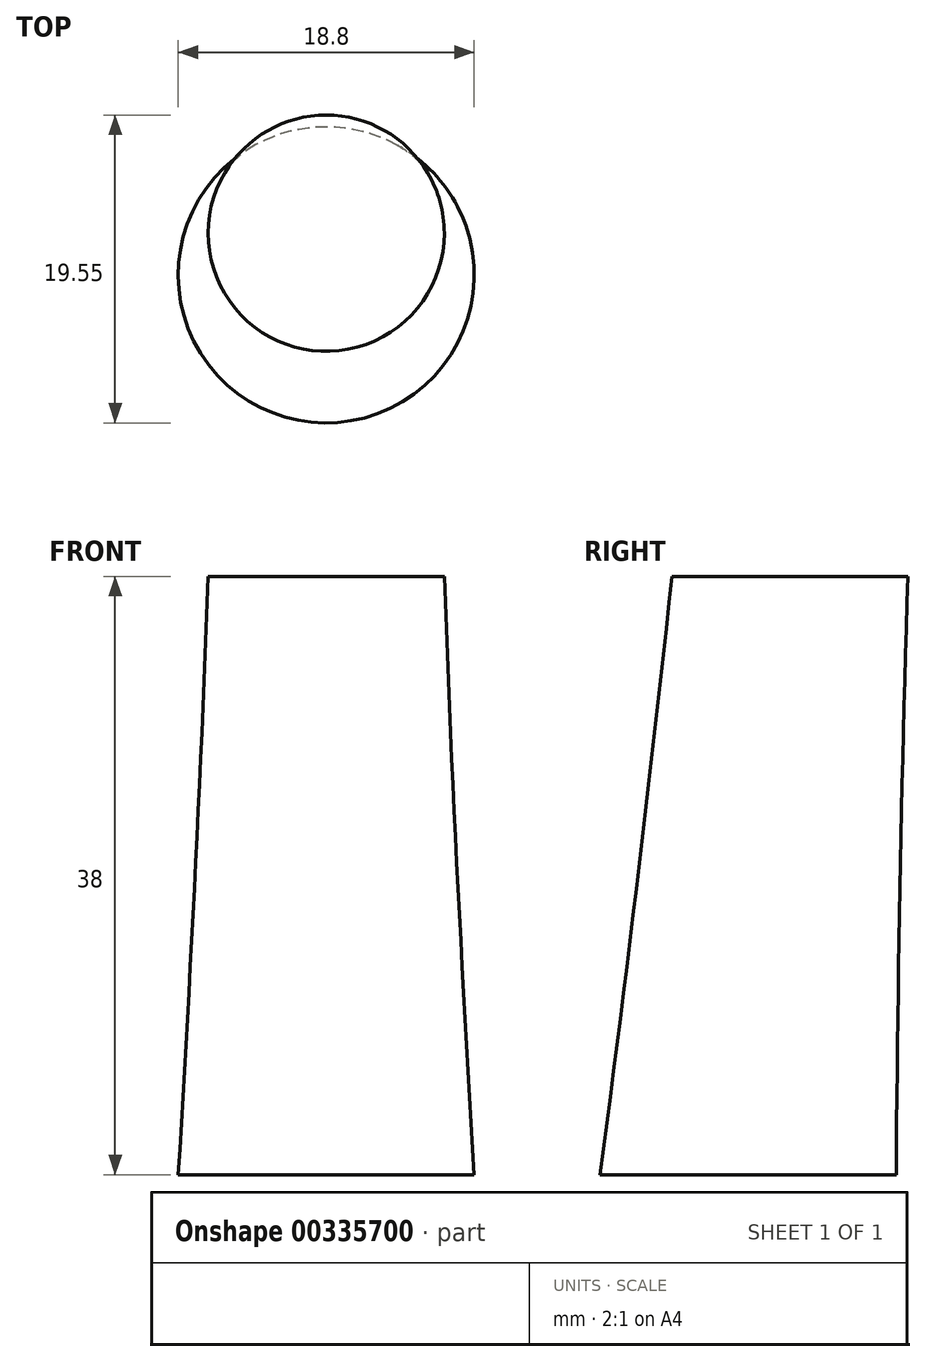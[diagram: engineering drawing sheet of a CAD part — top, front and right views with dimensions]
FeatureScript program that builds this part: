
annotation { "Feature Type Name" : "Feature", "Feature Type Description" : "" }
export const myFeature = defineFeature(function(context is Context, id is Id, definition is map)
    precondition{}
    {
        {
            var Q0;
            Q0=qCreatedBy(makeId("Top.planeOp"),FACE);
            cPlane(context, id + "F0", {"entities" : qUnion([Q0]), "cplaneType" : CPlaneType.OFFSET, "offset" : 38 * mm, "width" : 150 * mm, "height" : 150 * mm});
        }
        {
            var Q0;
            Q0=qCreatedBy(makeId("Top.planeOp"),FACE);
            var sketch = newSketch(context, id + "F1", { "sketchPlane" : qUnion([Q0])});
            skCircle(sketch, "E0", {"center": v(0, 0) * mm, "radius": 9.4 * mm});
            skSolve(sketch);
        }
        {
            var Q0;
            Q0=qCreatedBy(id+"F0.planeOp",FACE);
            var sketch = newSketch(context, id + "F2", { "sketchPlane" : qUnion([Q0])});
            skCircle(sketch, "E1", {"center": v(0, 2.65) * mm, "radius": 7.5 * mm});
            skSolve(sketch);
        }
        {
            var Q0;
            Q0=makeQuery(id+"F2.imprint","IMPRINT",FACE,{"disambiguationData":[TD([[makeQuery(id+"F2.imprint","IMPRINT",EDGE,{"derivedFrom":sQuery(id+"F2.wireOp",EDGE,"E1")}),1.0]])]});
            var Q1;
            Q1=makeQuery(id+"F1.imprint","IMPRINT",FACE,{"disambiguationData":[TD([[makeQuery(id+"F1.imprint","IMPRINT",EDGE,{"derivedFrom":sQuery(id+"F1.wireOp",EDGE,"E0")}),1.0]])]});
            loft(context, id + "F3", {"sheetProfilesArray" : [{ "sheetProfileEntities" : qUnion([Q0]) }, { "sheetProfileEntities" : qUnion([Q1]) }]});
        }
    });
